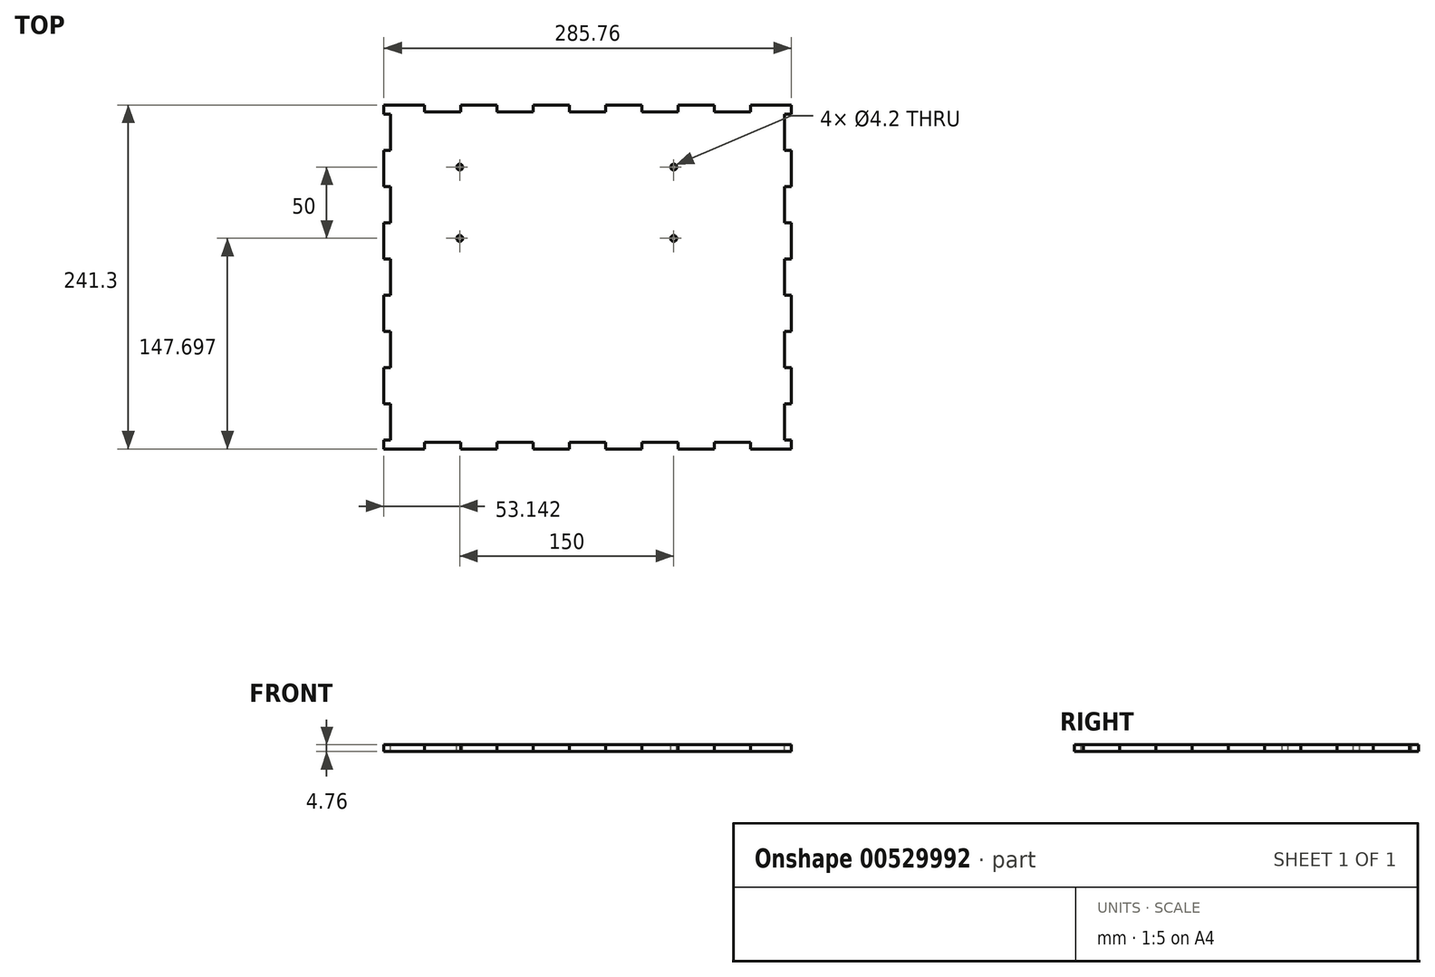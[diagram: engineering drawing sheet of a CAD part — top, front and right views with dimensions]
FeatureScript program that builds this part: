
annotation { "Feature Type Name" : "Feature", "Feature Type Description" : "" }
export const myFeature = defineFeature(function(context is Context, id is Id, definition is map)
    precondition{}
    {
        {
            var Q0;
            Q0=qCreatedBy(makeId("Top.planeOp"),FACE);
            var sketch = newSketch(context, id + "F0", { "sketchPlane" : qUnion([Q0])});
            skLineSegment(sketch, "E0.bottom", {"start": v(-142.87, 120.65) * mm, "end": v(142.88, 120.65) * mm});
            skLineSegment(sketch, "E0.top", {"start": v(-142.88, -120.65) * mm, "end": v(142.87, -120.65) * mm});
            skLineSegment(sketch, "E0.left", {"start": v(-142.87, 120.65) * mm, "end": v(-142.88, -120.65) * mm});
            skLineSegment(sketch, "E0.right", {"start": v(142.88, 120.65) * mm, "end": v(142.87, -120.65) * mm});
            skPoint(sketch, "E0.middle", {"position": v(0, 0) * mm});
            skSolve(sketch);
        }
        {
            var Q0;
            Q0 = qSketchRegion(id + "F0", true);
            extrude(context, id + "F1", {"entities" : qUnion([Q0]), "depth" : 4.76 * mm, "offsetDistance" : 25.4 * mm});
        }
        {
            var Q0;
            Q0=makeQuery(id+"F1.opExtrude","CAP_FACE",FACE,{"disambiguationData":[OSD([sQuery(id+"F0.wireOp",EDGE,"E0.bottom"),sQuery(id+"F0.wireOp",EDGE,"E0.top"),sQuery(id+"F0.wireOp",EDGE,"E0.left"),sQuery(id+"F0.wireOp",EDGE,"E0.right")])],"isStart":false});
            var sketch = newSketch(context, id + "F2", { "sketchPlane" : qUnion([Q0])});
            skCircle(sketch, "E1", {"center": v(-89.74, 77.05) * mm, "radius": 2.1 * mm});
            skCircle(sketch, "E2.0.1.0", {"center": v(-89.74, 27.05) * mm, "radius": 2.1 * mm});
            skCircle(sketch, "E2.1.0.0", {"center": v(60.26, 77.05) * mm, "radius": 2.1 * mm});
            skCircle(sketch, "E2.1.1.0", {"center": v(60.26, 27.05) * mm, "radius": 2.1 * mm});
            skLineSegment(sketch, "E2.direction1", {"start": v(-89.74, 77.05) * mm, "end": v(60.26, 77.05) * mm, "construction": true});
            skLineSegment(sketch, "E2.direction2", {"start": v(-89.74, 77.05) * mm, "end": v(-89.74, 27.05) * mm, "construction": true});
            skSolve(sketch);
        }
        {
            var Q0;
            Q0 = qSketchRegion(id + "F2", true);
            extrude(context, id + "F3", {"entities" : qUnion([Q0]), "operationType" : NewBodyOperationType.REMOVE, "oppositeDirection" : true, "depth" : 25.4 * mm, "offsetDistance" : 25.4 * mm});
        }
        {
            var Q0;
            Q0=makeQuery(id+"F1.opExtrude","CAP_FACE",FACE,{"disambiguationData":[OSD([sQuery(id+"F0.wireOp",EDGE,"E0.bottom"),sQuery(id+"F0.wireOp",EDGE,"E0.top"),sQuery(id+"F0.wireOp",EDGE,"E0.left"),sQuery(id+"F0.wireOp",EDGE,"E0.right")])],"isStart":false});
            var sketch = newSketch(context, id + "F4", { "sketchPlane" : qUnion([Q0])});
            skLineSegment(sketch, "E3", {"start": v(0, 0) * mm, "end": v(0, -120.65) * mm, "construction": true});
            skLineSegment(sketch, "E4.bottom", {"start": v(-12.7, -115.89) * mm, "end": v(12.7, -115.89) * mm});
            skLineSegment(sketch, "E4.top", {"start": v(-12.7, -120.65) * mm, "end": v(12.7, -120.65) * mm});
            skLineSegment(sketch, "E4.left", {"start": v(-12.7, -115.89) * mm, "end": v(-12.7, -120.65) * mm});
            skLineSegment(sketch, "E4.right", {"start": v(12.7, -115.89) * mm, "end": v(12.7, -120.65) * mm});
            skLineSegment(sketch, "E5", {"start": v(0, -115.89) * mm, "end": v(0, -120.65) * mm, "construction": true});
            skLineSegment(sketch, "E6.1.0.0", {"start": v(50.8, -115.89) * mm, "end": v(50.8, -120.65) * mm, "construction": true});
            skLineSegment(sketch, "E6.1.0.1", {"start": v(38.1, -115.89) * mm, "end": v(63.5, -115.89) * mm});
            skLineSegment(sketch, "E6.1.0.2", {"start": v(38.1, -115.89) * mm, "end": v(38.1, -120.65) * mm});
            skLineSegment(sketch, "E6.1.0.3", {"start": v(63.5, -115.89) * mm, "end": v(63.5, -120.65) * mm});
            skLineSegment(sketch, "E6.1.0.4", {"start": v(38.1, -120.65) * mm, "end": v(63.5, -120.65) * mm});
            skLineSegment(sketch, "E6.2.0.0", {"start": v(101.6, -115.89) * mm, "end": v(101.6, -120.65) * mm, "construction": true});
            skLineSegment(sketch, "E6.2.0.1", {"start": v(88.9, -115.89) * mm, "end": v(114.3, -115.89) * mm});
            skLineSegment(sketch, "E6.2.0.2", {"start": v(88.9, -115.89) * mm, "end": v(88.9, -120.65) * mm});
            skLineSegment(sketch, "E6.2.0.3", {"start": v(114.3, -115.89) * mm, "end": v(114.3, -120.65) * mm});
            skLineSegment(sketch, "E6.2.0.4", {"start": v(88.9, -120.65) * mm, "end": v(114.3, -120.65) * mm});
            skLineSegment(sketch, "E6.direction1", {"start": v(0, -120.65) * mm, "end": v(50.8, -120.65) * mm, "construction": true});
            skLineSegment(sketch, "E7.1.0.0", {"start": v(-50.8, -115.89) * mm, "end": v(-50.8, -120.65) * mm, "construction": true});
            skLineSegment(sketch, "E7.1.0.1", {"start": v(-63.5, -115.89) * mm, "end": v(-38.1, -115.89) * mm});
            skLineSegment(sketch, "E7.1.0.2", {"start": v(-63.5, -115.89) * mm, "end": v(-63.5, -120.65) * mm});
            skLineSegment(sketch, "E7.1.0.3", {"start": v(-38.1, -115.89) * mm, "end": v(-38.1, -120.65) * mm});
            skLineSegment(sketch, "E7.1.0.4", {"start": v(-63.5, -120.65) * mm, "end": v(-38.1, -120.65) * mm});
            skLineSegment(sketch, "E7.2.0.0", {"start": v(-101.6, -115.89) * mm, "end": v(-101.6, -120.65) * mm, "construction": true});
            skLineSegment(sketch, "E7.2.0.1", {"start": v(-114.3, -115.89) * mm, "end": v(-88.9, -115.89) * mm});
            skLineSegment(sketch, "E7.2.0.2", {"start": v(-114.3, -115.89) * mm, "end": v(-114.3, -120.65) * mm});
            skLineSegment(sketch, "E7.2.0.3", {"start": v(-88.9, -115.89) * mm, "end": v(-88.9, -120.65) * mm});
            skLineSegment(sketch, "E7.2.0.4", {"start": v(-114.3, -120.65) * mm, "end": v(-88.9, -120.65) * mm});
            skLineSegment(sketch, "E7.direction1", {"start": v(0, -120.65) * mm, "end": v(-50.8, -120.65) * mm, "construction": true});
            skLineSegment(sketch, "E8", {"start": v(0, 0) * mm, "end": v(142.88, 0) * mm, "construction": true});
            skLineSegment(sketch, "E9.MirrorCS", {"start": v(-114.3, 115.89) * mm, "end": v(-114.3, 120.65) * mm});
            skLineSegment(sketch, "E10.MirrorCS", {"start": v(-114.3, 115.89) * mm, "end": v(-88.9, 115.89) * mm});
            skLineSegment(sketch, "E11.MirrorCS", {"start": v(-114.3, 120.65) * mm, "end": v(-88.9, 120.65) * mm});
            skLineSegment(sketch, "E12.MirrorCS", {"start": v(-88.9, 115.89) * mm, "end": v(-88.9, 120.65) * mm});
            skLineSegment(sketch, "E13.MirrorCS", {"start": v(-63.5, 115.89) * mm, "end": v(-63.5, 120.65) * mm});
            skLineSegment(sketch, "E14.MirrorCS", {"start": v(-63.5, 115.89) * mm, "end": v(-38.1, 115.89) * mm});
            skLineSegment(sketch, "E15.MirrorCS", {"start": v(-63.5, 120.65) * mm, "end": v(-38.1, 120.65) * mm});
            skLineSegment(sketch, "E16.MirrorCS", {"start": v(-38.1, 115.89) * mm, "end": v(-38.1, 120.65) * mm});
            skLineSegment(sketch, "E17.MirrorCS", {"start": v(-12.7, 115.89) * mm, "end": v(-12.7, 120.65) * mm});
            skLineSegment(sketch, "E18.MirrorCS", {"start": v(-12.7, 115.89) * mm, "end": v(12.7, 115.89) * mm});
            skLineSegment(sketch, "E19.MirrorCS", {"start": v(0, 120.65) * mm, "end": v(-50.8, 120.65) * mm, "construction": true});
            skLineSegment(sketch, "E20.MirrorCS", {"start": v(0, 120.65) * mm, "end": v(50.8, 120.65) * mm, "construction": true});
            skLineSegment(sketch, "E21.MirrorCS", {"start": v(12.7, 115.89) * mm, "end": v(12.7, 120.65) * mm});
            skLineSegment(sketch, "E22.MirrorCS", {"start": v(38.1, 115.89) * mm, "end": v(38.1, 120.65) * mm});
            skLineSegment(sketch, "E23.MirrorCS", {"start": v(38.1, 115.89) * mm, "end": v(63.5, 115.89) * mm});
            skLineSegment(sketch, "E24.MirrorCS", {"start": v(38.1, 120.65) * mm, "end": v(63.5, 120.65) * mm});
            skLineSegment(sketch, "E25.MirrorCS", {"start": v(63.5, 115.89) * mm, "end": v(63.5, 120.65) * mm});
            skLineSegment(sketch, "E26.MirrorCS", {"start": v(88.9, 115.89) * mm, "end": v(88.9, 120.65) * mm});
            skLineSegment(sketch, "E27.MirrorCS", {"start": v(88.9, 120.65) * mm, "end": v(114.3, 120.65) * mm});
            skLineSegment(sketch, "E28.MirrorCS", {"start": v(88.9, 115.89) * mm, "end": v(114.3, 115.89) * mm});
            skLineSegment(sketch, "E29.MirrorCS", {"start": v(114.3, 115.89) * mm, "end": v(114.3, 120.65) * mm});
            skLineSegment(sketch, "E30", {"start": v(-12.7, 120.65) * mm, "end": v(12.7, 120.65) * mm});
            skLineSegment(sketch, "E31.bottom", {"start": v(142.88, 12.7) * mm, "end": v(138.11, 12.7) * mm});
            skLineSegment(sketch, "E31.top", {"start": v(142.88, -12.7) * mm, "end": v(138.11, -12.7) * mm});
            skLineSegment(sketch, "E31.left", {"start": v(142.88, -12.7) * mm, "end": v(142.88, 12.7) * mm});
            skLineSegment(sketch, "E31.right", {"start": v(138.11, -12.7) * mm, "end": v(138.11, 12.7) * mm});
            skPoint(sketch, "E31.middle", {"position": v(140.5, 0) * mm});
            skLineSegment(sketch, "E32", {"start": v(138.11, 0) * mm, "end": v(142.88, 0) * mm, "construction": true});
            skLineSegment(sketch, "E33.0.1.0", {"start": v(138.11, 50.8) * mm, "end": v(142.88, 50.8) * mm, "construction": true});
            skLineSegment(sketch, "E33.0.1.1", {"start": v(138.11, 38.1) * mm, "end": v(138.11, 63.5) * mm});
            skLineSegment(sketch, "E33.0.1.2", {"start": v(142.88, 63.5) * mm, "end": v(138.11, 63.5) * mm});
            skLineSegment(sketch, "E33.0.1.3", {"start": v(142.88, 38.1) * mm, "end": v(142.88, 63.5) * mm});
            skLineSegment(sketch, "E33.0.1.4", {"start": v(142.88, 38.1) * mm, "end": v(138.11, 38.1) * mm});
            skLineSegment(sketch, "E33.0.2.0", {"start": v(138.11, 101.6) * mm, "end": v(142.88, 101.6) * mm, "construction": true});
            skLineSegment(sketch, "E33.0.2.1", {"start": v(138.11, 88.9) * mm, "end": v(138.11, 114.3) * mm});
            skLineSegment(sketch, "E33.0.2.2", {"start": v(142.88, 114.3) * mm, "end": v(138.11, 114.3) * mm});
            skLineSegment(sketch, "E33.0.2.3", {"start": v(142.88, 88.9) * mm, "end": v(142.88, 114.3) * mm});
            skLineSegment(sketch, "E33.0.2.4", {"start": v(142.88, 88.9) * mm, "end": v(138.11, 88.9) * mm});
            skLineSegment(sketch, "E33.direction1", {"start": v(138.11, 0) * mm, "end": v(153.99, 0) * mm, "construction": true});
            skLineSegment(sketch, "E33.direction2", {"start": v(138.11, 0) * mm, "end": v(138.11, 50.8) * mm, "construction": true});
            skLineSegment(sketch, "E34.0.1.0", {"start": v(138.11, -50.8) * mm, "end": v(153.99, -50.8) * mm, "construction": true});
            skLineSegment(sketch, "E34.0.1.1", {"start": v(138.11, -63.5) * mm, "end": v(138.11, -38.1) * mm});
            skLineSegment(sketch, "E34.0.1.2", {"start": v(142.88, -38.1) * mm, "end": v(138.11, -38.1) * mm});
            skLineSegment(sketch, "E34.0.1.3", {"start": v(142.88, -63.5) * mm, "end": v(142.88, -38.1) * mm});
            skLineSegment(sketch, "E34.0.1.4", {"start": v(142.88, -63.5) * mm, "end": v(138.11, -63.5) * mm});
            skLineSegment(sketch, "E34.0.2.0", {"start": v(138.11, -101.6) * mm, "end": v(153.99, -101.6) * mm, "construction": true});
            skLineSegment(sketch, "E34.0.2.1", {"start": v(138.11, -114.3) * mm, "end": v(138.11, -88.9) * mm});
            skLineSegment(sketch, "E34.0.2.2", {"start": v(142.88, -88.9) * mm, "end": v(138.11, -88.9) * mm});
            skLineSegment(sketch, "E34.0.2.3", {"start": v(142.88, -114.3) * mm, "end": v(142.88, -88.9) * mm});
            skLineSegment(sketch, "E34.0.2.4", {"start": v(142.88, -114.3) * mm, "end": v(138.11, -114.3) * mm});
            skLineSegment(sketch, "E34.direction2", {"start": v(138.11, 0) * mm, "end": v(138.11, -50.8) * mm, "construction": true});
            skLineSegment(sketch, "E35.MirrorCS", {"start": v(-142.88, 114.3) * mm, "end": v(-138.11, 114.3) * mm});
            skLineSegment(sketch, "E36.MirrorCS", {"start": v(-142.88, 88.9) * mm, "end": v(-138.11, 88.9) * mm});
            skLineSegment(sketch, "E37.MirrorCS", {"start": v(-142.88, 38.1) * mm, "end": v(-138.11, 38.1) * mm});
            skLineSegment(sketch, "E38.MirrorCS", {"start": v(-142.88, 63.5) * mm, "end": v(-138.11, 63.5) * mm});
            skLineSegment(sketch, "E39.MirrorCS", {"start": v(-138.11, 50.8) * mm, "end": v(-142.88, 50.8) * mm, "construction": true});
            skLineSegment(sketch, "E40.MirrorCS", {"start": v(-138.11, 101.6) * mm, "end": v(-142.88, 101.6) * mm, "construction": true});
            skLineSegment(sketch, "E41.MirrorCS", {"start": v(-138.11, 88.9) * mm, "end": v(-138.11, 114.3) * mm});
            skLineSegment(sketch, "E42.MirrorCS", {"start": v(-142.88, 88.9) * mm, "end": v(-142.88, 114.3) * mm});
            skLineSegment(sketch, "E43.MirrorCS", {"start": v(-142.88, 38.1) * mm, "end": v(-142.88, 63.5) * mm});
            skLineSegment(sketch, "E44.MirrorCS", {"start": v(-138.11, 38.1) * mm, "end": v(-138.11, 63.5) * mm});
            skLineSegment(sketch, "E45.MirrorCS", {"start": v(-138.11, 0) * mm, "end": v(-142.88, 0) * mm, "construction": true});
            skLineSegment(sketch, "E46.MirrorCS", {"start": v(-142.88, -12.7) * mm, "end": v(-142.88, 12.7) * mm});
            skLineSegment(sketch, "E47.MirrorCS", {"start": v(-138.11, -63.5) * mm, "end": v(-138.11, -38.1) * mm});
            skLineSegment(sketch, "E48.MirrorCS", {"start": v(-138.11, -12.7) * mm, "end": v(-138.11, 12.7) * mm});
            skLineSegment(sketch, "E49.MirrorCS", {"start": v(-142.88, -38.1) * mm, "end": v(-138.11, -38.1) * mm});
            skLineSegment(sketch, "E50.MirrorCS", {"start": v(-142.88, -12.7) * mm, "end": v(-138.11, -12.7) * mm});
            skLineSegment(sketch, "E51.MirrorCS", {"start": v(-142.88, -114.3) * mm, "end": v(-138.11, -114.3) * mm});
            skLineSegment(sketch, "E52.MirrorCS", {"start": v(-142.88, -63.5) * mm, "end": v(-142.88, -38.1) * mm});
            skLineSegment(sketch, "E53.MirrorCS", {"start": v(-142.88, -88.9) * mm, "end": v(-138.11, -88.9) * mm});
            skLineSegment(sketch, "E54.MirrorCS", {"start": v(-142.88, -63.5) * mm, "end": v(-138.11, -63.5) * mm});
            skLineSegment(sketch, "E55.MirrorCS", {"start": v(-142.88, 12.7) * mm, "end": v(-138.11, 12.7) * mm});
            skLineSegment(sketch, "E56.MirrorCS", {"start": v(-138.11, 0) * mm, "end": v(-153.99, 0) * mm, "construction": true});
            skLineSegment(sketch, "E57.MirrorCS", {"start": v(-142.88, -114.3) * mm, "end": v(-142.88, -88.9) * mm});
            skLineSegment(sketch, "E58.MirrorCS", {"start": v(-138.11, -114.3) * mm, "end": v(-138.11, -88.9) * mm});
            skLineSegment(sketch, "E59.MirrorCS", {"start": v(-138.11, 0) * mm, "end": v(-138.11, -50.8) * mm, "construction": true});
            skPoint(sketch, "E60.MirrorP", {"position": v(-140.5, 0) * mm});
            skLineSegment(sketch, "E61.MirrorCS", {"start": v(-138.11, -50.8) * mm, "end": v(-153.99, -50.8) * mm, "construction": true});
            skLineSegment(sketch, "E62.MirrorCS", {"start": v(-138.11, -101.6) * mm, "end": v(-153.99, -101.6) * mm, "construction": true});
            skSolve(sketch);
        }
        {
            var Q0;
            Q0 = qSketchRegion(id + "F4", true);
            extrude(context, id + "F5", {"entities" : qUnion([Q0]), "operationType" : NewBodyOperationType.REMOVE, "oppositeDirection" : true, "depth" : 25.4 * mm, "offsetDistance" : 25.4 * mm});
        }
    });
